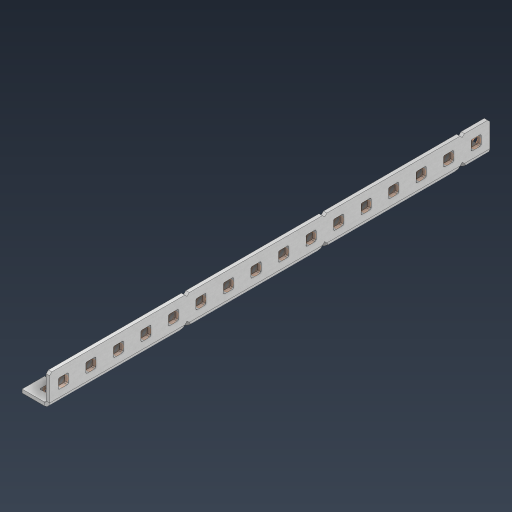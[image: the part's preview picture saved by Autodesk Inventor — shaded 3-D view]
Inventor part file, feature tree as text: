
AUTODESK INVENTOR PART (.ipt)
format: ipt  version: 2024.3 (Build 283343000, 343)  size: 760,832 bytes
history: native  units: in
note: dims shown in document units (in); Inventor stores cm internally (conversion verified against a paired STEP export)
features: other x55, extrude x46, sheet_metal_op x11, pattern_linear x2, mirror x1, chamfer x1, sketch x1
ambient origin geometry x8: Origin, YZ Plane, XZ Plane, XY Plane, X Axis, Y Axis, Z Axis, Center Point
bodies: Solid1 (feature_tree), Body (feature_tree)
feature tree (117):
  sheet_metal_op  "Flanges"
  other  "Flange Pattern Plane"
  other  "Flange Pattern Sketch"
  sheet_metal_op  "Flange Pattern"
  sheet_metal_op  "Body Pattern"
  pattern_linear  "Center Pattern"  Spacing1=8.0in  [1 undecoded]
  other  "Arc Length"
  mirror  "Notch Mirror"
  pattern_linear  "Notch Pattern"  Spacing1=0.0625in  [1 undecoded]
  chamfer  "End Chamfer"
  extrude  "Half Cut"  Depth=0.0625in
  other  "Plate1"
  sketch  "Sketch2"  dims[d0=1.0in d1=8.0in d2=0.0625in d3=0.0625in d4=0.0312in d5=0.125in d6=0.0625in d7=0.5in d8=90.0deg d9=0.0312in d10=0.25in d11=0.0625in d12=0.0625in d16=0.182in d17=0.02in d18=0.0625in d19=0.0in d20=0.25in d21=0.25in d38=6.2992in d40=0.5in d41=0.3937in d43=1.0in d46=0.172in d47=1.0in d48=0.0in d49=0.182in d50=0.02in d51=0.25in d52=0.25in d53=0.0625in d54=0.0in d55=0.172in d56=1.0in d57=0.0in d58=0.25in d60=6.2992in d62=0.5in d63=0.3937in d65=0.5in d85=0.1473in d86=0.1782in d88=0.04in d89=0.0625in d90=0.0in d91=0.04in d92=0.0491in d95=2.5in d96=0.04in d97=0.25in d98=45.0deg d99=0.25in d100=0.5in d101=0.0in d102=2.497in d106=0.182in d107=0.02in d108=0.5in d109=0.5in d110=0.0625in d111=0.0in d112=0.172in d113=0.5in d114=0.0in d117=0.5in d118=0.5in d119=0.5in]
  other  "Plate2"
  sheet_metal_op  "Bend1"
  sheet_metal_op  "Corner1"
  other  "Srf1"
  other  "Srf2"
  other  "Srf91"
  sheet_metal_op  "Body Pattern Sketch"
  other  "Srf92"
  other  "Srf786"
  other  "Srf823"
  other  "Srf824"
  other  "Srf825"
  other  "Srf826"
  other  "Srf827"
  other  "Srf828"
  other  "Srf829"
  other  "Srf856"
  other  "Srf857"
  other  "Srf858"
  other  "Srf859"
  other  "Srf860"
  other  "Srf861"
  other  "Srf862"
  other  "Srf889"
  other  "Srf890"
  other  "Srf891"
  other  "Srf892"
  other  "Srf893"
  other  "Srf894"
  other  "Srf895"
  other  "Srf896"
  other  "Srf922"
  other  "Srf923"
  other  "Srf924"
  other  "Srf925"
  other  "Srf926"
  other  "Srf959"
  other  "Srf960"
  other  "Srf961"
  other  "Srf962"
  other  "Srf963"
  other  "Srf996"
  other  "Srf997"
  other  "Srf998"
  other  "Srf999"
  other  "Srf1000"
  other  "Srf1143"
  other  "Srf1144"
  other  "Srf1199"
  other  "Srf1200"
  other  "Srf1255"
  other  "Srf1256"
  sheet_metal_op  "Flange Stamp"
  sheet_metal_op  "Flange Circle"
  sheet_metal_op  "Body Stamp"
  sheet_metal_op  "Body Circle"
  other  "Center Stamp"
  other  "Center Circle"
  sheet_metal_op  "Notch"
  extrude  "ExtrusionSrf2"  Depth=0.0312in
  extrude  "ExtrusionSrf92"  Depth=0.5in
  extrude  "ExtrusionSrf823"  Depth=0.0625in
  extrude  "ExtrusionSrf824"  Depth=0.5in TaperAngle=90.0deg
  extrude  "ExtrusionSrf825"  Depth=0.25in
  extrude  "ExtrusionSrf826"  Depth=0.0625in
  extrude  "ExtrusionSrf827"  Depth=0.0625in
  extrude  "ExtrusionSrf828"  Depth=0.182in
  extrude  "ExtrusionSrf829"  Depth=0.02in
  extrude  "ExtrusionSrf856"  Depth=0.0625in
  extrude  "ExtrusionSrf857"  TaperAngle=0.0deg  [1 undecoded]
  extrude  "ExtrusionSrf858"  Depth=0.25in
  extrude  "ExtrusionSrf859"  Depth=0.25in
  extrude  "ExtrusionSrf860"  Depth=0.5in
  extrude  "ExtrusionSrf861"  Depth=0.5in
  extrude  "ExtrusionSrf862"  Depth=1.0in TaperAngle=0.0deg
  extrude  "ExtrusionSrf889"  Depth=0.182in
  extrude  "ExtrusionSrf890"  Depth=0.02in
  extrude  "ExtrusionSrf891"  Depth=0.25in
  extrude  "ExtrusionSrf892"  Depth=0.25in
  extrude  "ExtrusionSrf893"  Depth=0.0625in
  extrude  "ExtrusionSrf894"  TaperAngle=0.0deg  [1 undecoded]
  extrude  "ExtrusionSrf895"  Depth=0.5in
  extrude  "ExtrusionSrf896"  Depth=1.0in TaperAngle=0.0deg
  extrude  "ExtrusionSrf922"  Depth=0.25in
  extrude  "ExtrusionSrf923"  Depth=0.5in
  extrude  "ExtrusionSrf924"  Depth=0.5in
  extrude  "ExtrusionSrf925"  Depth=0.5in
  extrude  "ExtrusionSrf926"  Depth=0.5in
  extrude  "ExtrusionSrf959"  Depth=0.5in
  extrude  "ExtrusionSrf960"  Depth=0.0625in
  extrude  "ExtrusionSrf961"  TaperAngle=0.0deg  [1 undecoded]
  extrude  "ExtrusionSrf962"  Depth=0.5in
  extrude  "ExtrusionSrf963"  Depth=0.5in
  extrude  "ExtrusionSrf996"  Depth=2.5in
  extrude  "ExtrusionSrf997"  Depth=0.25in TaperAngle=45.0deg
  extrude  "ExtrusionSrf998"  Depth=0.25in
  extrude  "ExtrusionSrf999"  Depth=0.5in TaperAngle=0.0deg
  extrude  "ExtrusionSrf1000"  Depth=0.5in
  extrude  "ExtrusionSrf1143"  Depth=0.182in
  extrude  "ExtrusionSrf1144"  Depth=0.02in
  extrude  "ExtrusionSrf1199"  Depth=0.5in
  extrude  "ExtrusionSrf1200"  Depth=0.5in
  extrude  "ExtrusionSrf1255"  Depth=0.0625in
  extrude  "ExtrusionSrf1256"  TaperAngle=0.0deg  [1 undecoded]
note: 6 required parameter values undecoded (feature->parameter linkage not recoverable at this tier; creation-order binding heuristic only, values carry confidence <= 0.55)
